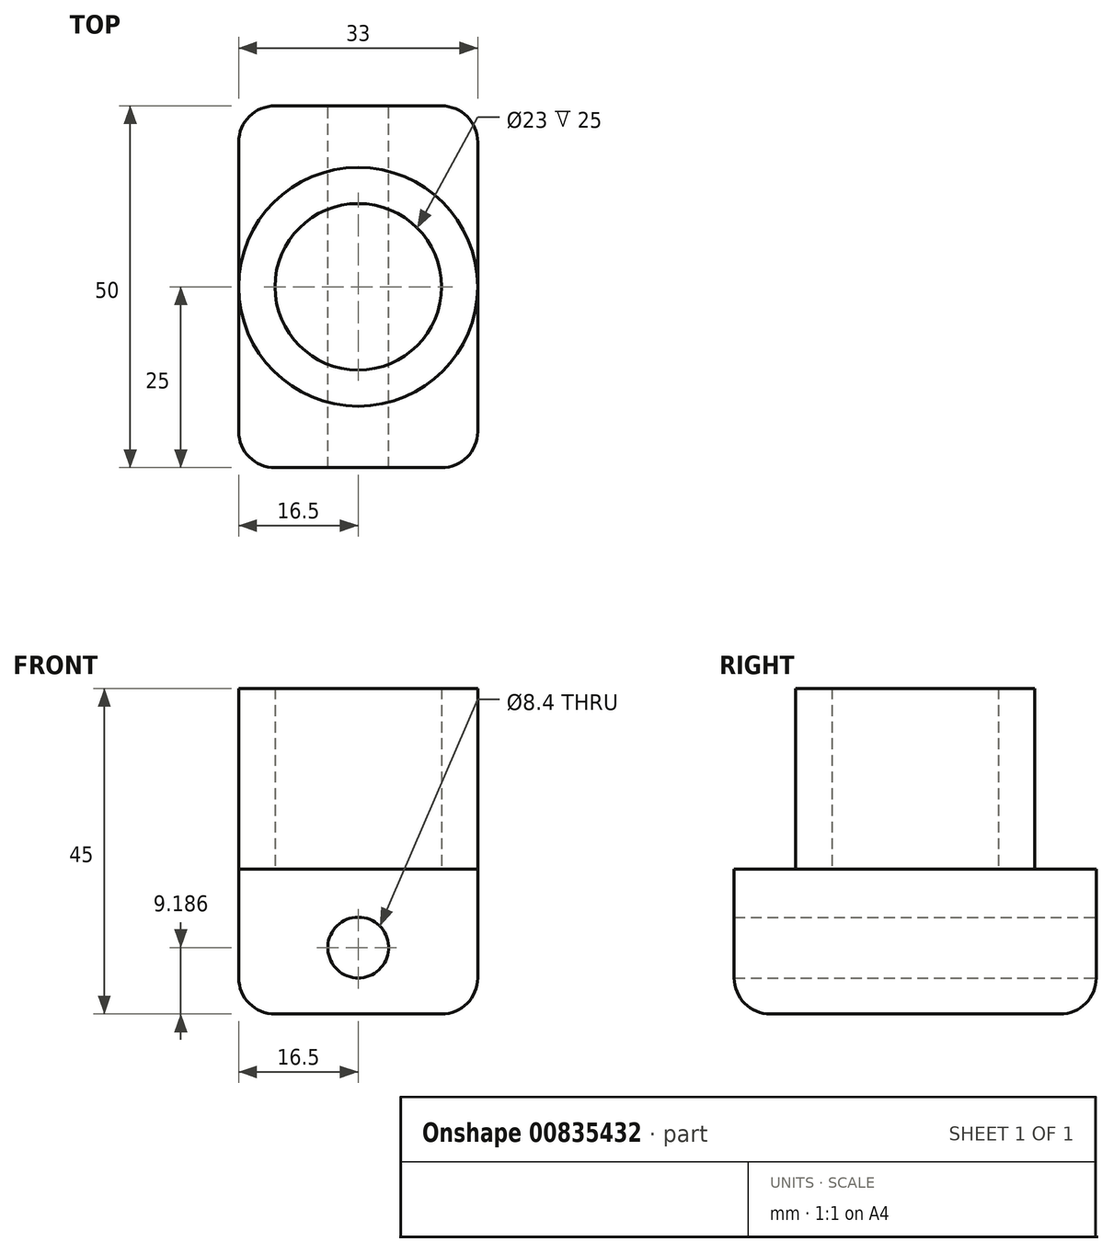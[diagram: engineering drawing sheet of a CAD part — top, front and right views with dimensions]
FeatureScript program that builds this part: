
annotation { "Feature Type Name" : "Feature", "Feature Type Description" : "" }
export const myFeature = defineFeature(function(context is Context, id is Id, definition is map)
    precondition{}
    {
        {
            var Q0;
            Q0=qCreatedBy(makeId("Top.planeOp"),FACE);
            var sketch = newSketch(context, id + "F0", { "sketchPlane" : qUnion([Q0])});
            skCircle(sketch, "E0", {"center": v(0, 0) * mm, "radius": 11.5 * mm});
            skCircle(sketch, "E1.0", {"center": v(0, 0) * mm, "radius": 16.5 * mm});
            skSolve(sketch);
        }
        {
            var Q0;
            Q0 = qSketchRegion(id + "F0", true);
            extrude(context, id + "F1", {"entities" : qUnion([Q0]), "depth" : 25 * mm, "offsetDistance" : 25 * mm});
        }
        {
            var Q0;
            Q0=qCreatedBy(makeId("Top.planeOp"),FACE);
            var sketch = newSketch(context, id + "F2", { "sketchPlane" : qUnion([Q0])});
            skLineSegment(sketch, "E2.bottom", {"start": v(-16.5, 25) * mm, "end": v(16.5, 25) * mm});
            skLineSegment(sketch, "E2.top", {"start": v(-16.5, -25) * mm, "end": v(16.5, -25) * mm});
            skLineSegment(sketch, "E2.left", {"start": v(-16.5, 25) * mm, "end": v(-16.5, -25) * mm});
            skLineSegment(sketch, "E2.right", {"start": v(16.5, 25) * mm, "end": v(16.5, -25) * mm});
            skPoint(sketch, "E2.middle", {"position": v(0, 0) * mm});
            skSolve(sketch);
        }
        {
            var Q0;
            Q0 = qSketchRegion(id + "F2", true);
            extrude(context, id + "F3", {"entities" : qUnion([Q0]), "operationType" : NewBodyOperationType.ADD, "depth" : -20 * mm, "offsetDistance" : 25 * mm});
        }
        {
            var Q0;
            Q0=qCreatedBy(makeId("Front.planeOp"),FACE);
            var sketch = newSketch(context, id + "F4", { "sketchPlane" : qUnion([Q0])});
            skCircle(sketch, "E3", {"center": v(0, -10.81) * mm, "radius": 4.2 * mm});
            skSolve(sketch);
        }
        {
            var Q0;
            Q0=sQuery(id+"F4.wireOp",VERTEX,"E3.center");
            var Q1;
            Q1=makeQuery(id+"F1.opExtrude","SWEPT_BODY",BODY,{"disambiguationData":[OSD([sQuery(id+"F0.wireOp",EDGE,"E0"),sQuery(id+"F0.wireOp",EDGE,"E1.0")])]});
            hole(context, id + "F5", {"style" : HoleStyle.SIMPLE, "endStyle" : HoleEndStyle.THROUGH, "oppositeDirection" : true, "holeDiameter" : 8.4 * mm, "majorDiameter" : 5 * mm, "isTappedThrough" : true, "tappedDepth" : 12 * mm, "tapClearance" : 3, "locations" : qUnion([Q0]), "scope" : qUnion([Q1])});
        }
        {
            var Q0;
            Q0=sQuery(id+"F4.wireOp",VERTEX,"E3.center");
            var Q1;
            Q1=makeQuery(id+"F1.opExtrude","SWEPT_BODY",BODY,{"disambiguationData":[OSD([sQuery(id+"F0.wireOp",EDGE,"E0"),sQuery(id+"F0.wireOp",EDGE,"E1.0")])]});
            hole(context, id + "F6", {"style" : HoleStyle.SIMPLE, "endStyle" : HoleEndStyle.THROUGH, "holeDiameter" : 8.4 * mm, "majorDiameter" : 5 * mm, "isTappedThrough" : true, "tappedDepth" : 12 * mm, "tapClearance" : 3, "locations" : qUnion([Q0]), "scope" : qUnion([Q1])});
        }
        {
            var Q0;
            Q0=makeQuery(id+"F3.opExtrude","CAP_FACE",FACE,{"disambiguationData":[OSD([sQuery(id+"F2.wireOp",EDGE,"E2.bottom"),sQuery(id+"F2.wireOp",EDGE,"E2.top"),sQuery(id+"F2.wireOp",EDGE,"E2.left"),sQuery(id+"F2.wireOp",EDGE,"E2.right")])],"isStart":false});
            var Q1;
            Q1=makeQuery(id+"F3.opExtrude","SWEPT_EDGE",EDGE,{"disambiguationData":[OSD([sQuery(id+"F2.wireOp",EDGE,"E2.bottom"),sQuery(id+"F2.wireOp",EDGE,"E2.left")])]});
            var Q2;
            Q2=makeQuery(id+"F3.opExtrude","SWEPT_EDGE",EDGE,{"disambiguationData":[OSD([sQuery(id+"F2.wireOp",EDGE,"E2.bottom"),sQuery(id+"F2.wireOp",EDGE,"E2.right")])]});
            var Q3;
            Q3=makeQuery(id+"F3.opExtrude","SWEPT_EDGE",EDGE,{"disambiguationData":[OSD([sQuery(id+"F2.wireOp",EDGE,"E2.top"),sQuery(id+"F2.wireOp",EDGE,"E2.right")])]});
            var Q4;
            Q4=makeQuery(id+"F3.opExtrude","SWEPT_EDGE",EDGE,{"disambiguationData":[OSD([sQuery(id+"F2.wireOp",EDGE,"E2.top"),sQuery(id+"F2.wireOp",EDGE,"E2.left")])]});
            fillet(context, id + "F7", {"entities" : qUnion([Q0, Q1, Q2, Q3, Q4]), "radius" : 5 * mm, "tangentPropagation" : true, "allowEdgeOverflow" : false});
        }
    });
